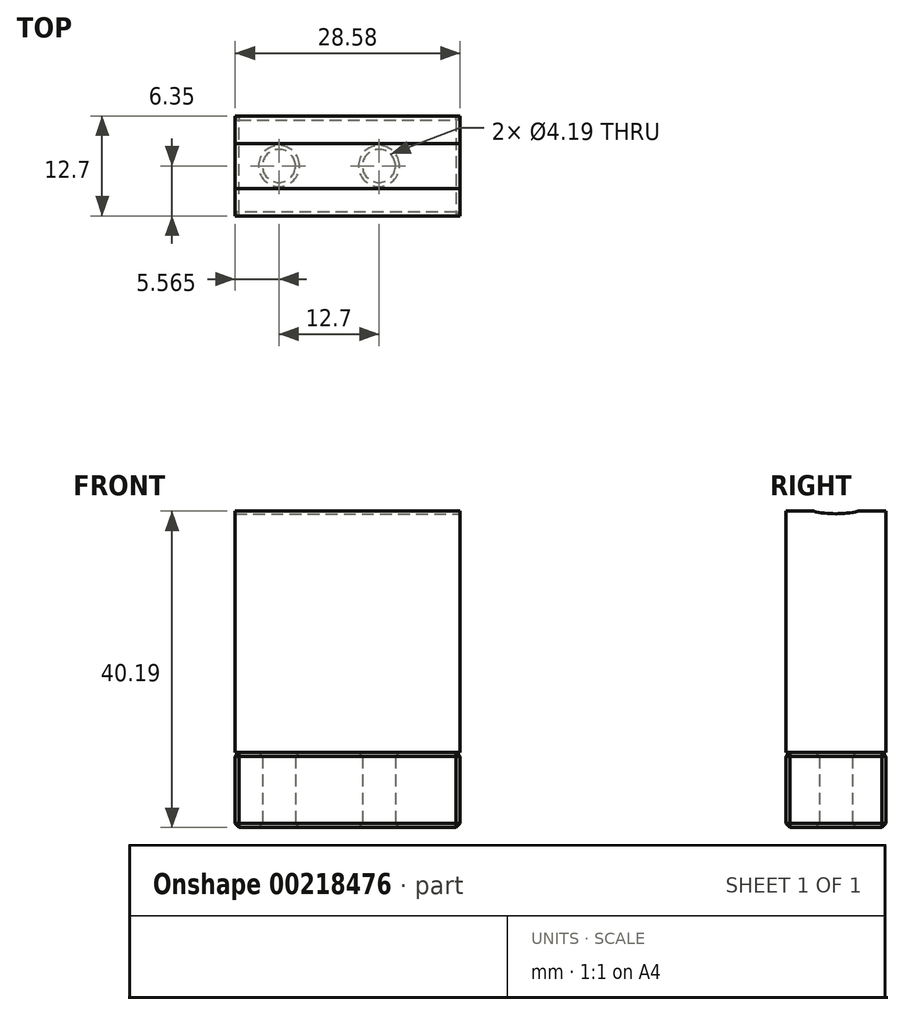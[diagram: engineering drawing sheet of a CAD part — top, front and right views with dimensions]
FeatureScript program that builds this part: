
annotation { "Feature Type Name" : "Feature", "Feature Type Description" : "" }
export const myFeature = defineFeature(function(context is Context, id is Id, definition is map)
    precondition{}
    {
        {
            var Q0;
            Q0=qCreatedBy(makeId("Top.planeOp"),FACE);
            var sketch = newSketch(context, id + "F0", { "sketchPlane" : qUnion([Q0])});
            skLineSegment(sketch, "E0.bottom", {"start": v(14.29, -6.35) * mm, "end": v(-14.29, -6.35) * mm});
            skLineSegment(sketch, "E0.top", {"start": v(14.29, 6.35) * mm, "end": v(-14.29, 6.35) * mm});
            skLineSegment(sketch, "E0.left", {"start": v(14.29, -6.35) * mm, "end": v(14.29, 6.35) * mm});
            skLineSegment(sketch, "E0.right", {"start": v(-14.29, -6.35) * mm, "end": v(-14.29, 6.35) * mm});
            skPoint(sketch, "E0.middle", {"position": v(0, 0) * mm});
            skSolve(sketch);
        }
        {
            var Q0;
            Q0 = qSketchRegion(id + "F0", true);
            extrude(context, id + "F1", {"entities" : qUnion([Q0]), "oppositeDirection" : true, "depth" : 9.52 * mm});
        }
        {
            var Q0;
            Q0=makeQuery(id+"F1.opExtrude","CAP_FACE",FACE,{"disambiguationData":[OSD([sQuery(id+"F0.wireOp",EDGE,"E0.bottom"),sQuery(id+"F0.wireOp",EDGE,"E0.top"),sQuery(id+"F0.wireOp",EDGE,"E0.left"),sQuery(id+"F0.wireOp",EDGE,"E0.right")])],"isStart":true});
            extrude(context, id + "F2", {"entities" : qUnion([Q0]), "depth" : 30.66 * mm});
        }
        {
            var Q0;
            Q0=qCreatedBy(makeId("Right.planeOp"),FACE);
            var sketch = newSketch(context, id + "F3", { "sketchPlane" : qUnion([Q0])});
            skCircle(sketch, "E1", {"center": v(0, 42.9) * mm, "radius": 12.57 * mm});
            skSolve(sketch);
        }
        {
            var Q0;
            Q0=makeQuery(id+"F3.imprint","IMPRINT",FACE,{"disambiguationData":[TD([[makeQuery(id+"F3.imprint","IMPRINT",EDGE,{"derivedFrom":sQuery(id+"F3.wireOp",EDGE,"E1")}),1.0]])]});
            extrude(context, id + "F4", {"entities" : qUnion([Q0]), "operationType" : NewBodyOperationType.REMOVE, "endBound" : BoundingType.THROUGH_ALL, "oppositeDirection" : true, "depth" : 25.4 * mm, "hasSecondDirection" : true, "secondDirectionBound" : SecondDirectionBoundingType.THROUGH_ALL, "secondDirectionOppositeDirection" : false, "secondDirectionDepth" : 25.4 * mm});
        }
        {
            var Q0;
            Q0=makeQuery(id+"F1.opExtrude","CAP_FACE",FACE,{"disambiguationData":[OSD([sQuery(id+"F0.wireOp",EDGE,"E0.bottom"),sQuery(id+"F0.wireOp",EDGE,"E0.top"),sQuery(id+"F0.wireOp",EDGE,"E0.left"),sQuery(id+"F0.wireOp",EDGE,"E0.right")])],"isStart":false});
            var sketch = newSketch(context, id + "F5", { "sketchPlane" : qUnion([Q0])});
            skCircle(sketch, "E2", {"center": v(-8.72, 0) * mm, "radius": 2.1 * mm});
            skCircle(sketch, "E3", {"center": v(3.98, 0) * mm, "radius": 2.1 * mm});
            skSolve(sketch);
        }
        {
            var Q0;
            Q0 = qSketchRegion(id + "F5", true);
            extrude(context, id + "F6", {"entities" : qUnion([Q0]), "operationType" : NewBodyOperationType.REMOVE, "endBound" : BoundingType.UP_TO_NEXT, "oppositeDirection" : true, "depth" : 25.4 * mm});
        }
        {
            var Q0;
            Q0=makeQuery(id+"F1.opExtrude","CAP_FACE",FACE,{"disambiguationData":[OSD([sQuery(id+"F0.wireOp",EDGE,"E0.bottom"),sQuery(id+"F0.wireOp",EDGE,"E0.top"),sQuery(id+"F0.wireOp",EDGE,"E0.left"),sQuery(id+"F0.wireOp",EDGE,"E0.right")])],"isStart":false});
            var Q1;
            Q1=makeQuery(id+"F1.opExtrude","CAP_FACE",FACE,{"disambiguationData":[OSD([sQuery(id+"F0.wireOp",EDGE,"E0.bottom"),sQuery(id+"F0.wireOp",EDGE,"E0.top"),sQuery(id+"F0.wireOp",EDGE,"E0.left"),sQuery(id+"F0.wireOp",EDGE,"E0.right")])],"isStart":true});
            var Q2;
            Q2=makeQuery(id+"F1.opExtrude","SWEPT_FACE",FACE,{"disambiguationData":[OSD([sQuery(id+"F0.wireOp",EDGE,"E0.bottom")])]});
            var Q3;
            Q3=makeQuery(id+"F1.opExtrude","SWEPT_FACE",FACE,{"disambiguationData":[OSD([sQuery(id+"F0.wireOp",EDGE,"E0.top")])]});
            chamfer(context, id + "F7", {"entities" : qUnion([Q0, Q1, Q2, Q3]), "width" : 0.5 * mm, "tangentPropagation" : true});
        }
    });
